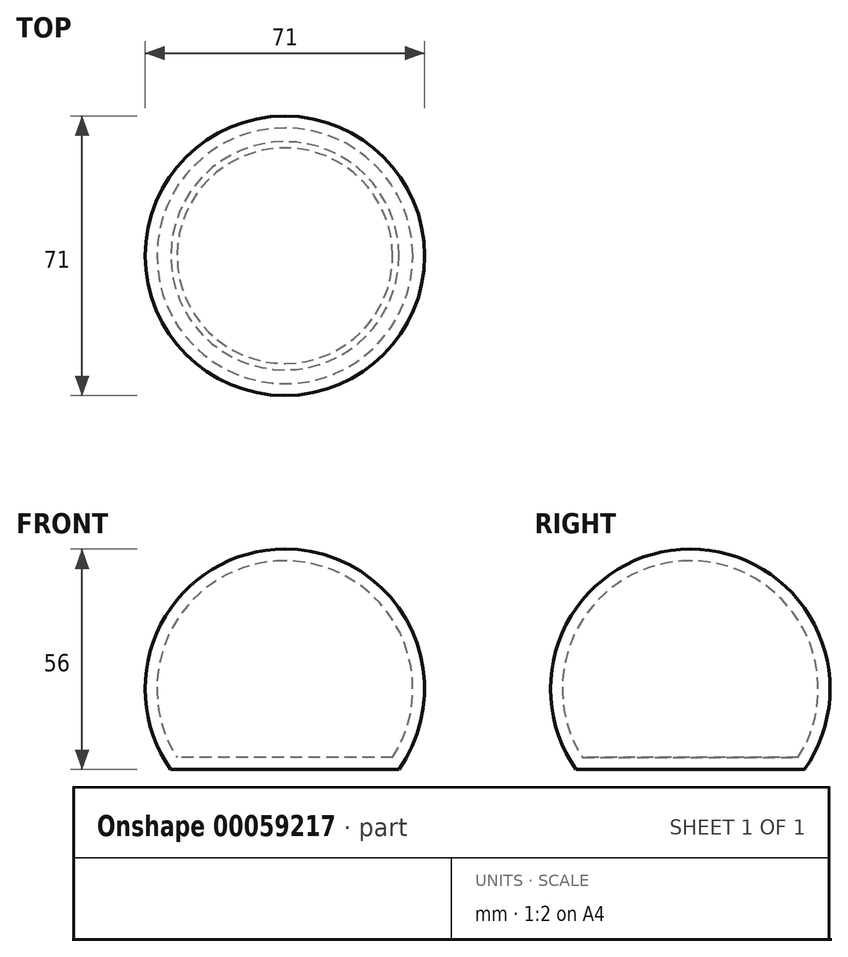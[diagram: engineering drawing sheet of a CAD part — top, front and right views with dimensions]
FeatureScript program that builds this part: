
annotation { "Feature Type Name" : "Feature", "Feature Type Description" : "" }
export const myFeature = defineFeature(function(context is Context, id is Id, definition is map)
    precondition{}
    {
        {
            var Q0;
            Q0=qCreatedBy(makeId("Front.planeOp"),FACE);
            var sketch = newSketch(context, id + "F0", { "sketchPlane" : qUnion([Q0])});
            skArc(sketch, "E0", {"start": v(27.39, -17.5) * mm, "mid": v(28.5, 15.61) * mm, "end": v(0, 32.5) * mm});
            skArc(sketch, "E1", {"start": v(28.98, -20.5) * mm, "mid": v(31.53, 16.32) * mm, "end": v(0, 35.5) * mm});
            skLineSegment(sketch, "E2", {"start": v(0, -17.5) * mm, "end": v(27.39, -17.5) * mm});
            skLineSegment(sketch, "E3", {"start": v(0, -20.5) * mm, "end": v(28.98, -20.5) * mm});
            skLineSegment(sketch, "E4", {"start": v(0, 53.72) * mm, "end": v(0, -43.65) * mm, "construction": true});
            skPoint(sketch, "E4.endSnap0", {"position": v(0, -20.5) * mm});
            skLineSegment(sketch, "E5", {"start": v(0, 35.5) * mm, "end": v(0, -20.5) * mm});
            skPoint(sketch, "E6.orphan", {"position": v(-28.98, -20.5) * mm});
            skSolve(sketch);
        }
        {
            var Q0;
            {var subQ3=sQuery(id+"F0.wireOp",EDGE,"E0");Q0=makeQuery(id+"F0.imprint","IMPRINT",FACE,{"disambiguationData":[TD([[makeQuery(id+"F0.imprint","IMPRINT",EDGE,{"derivedFrom":subQ3}),-1.0]])]});}
            var Q1;
            Q1=sQuery(id+"F0.wireOp",EDGE,"E4");
            revolve(context, id + "F1", {"entities" : qUnion([Q0]), "axis" : qUnion([Q1]), "revolveType" : RevolveType.FULL});
        }
    });
